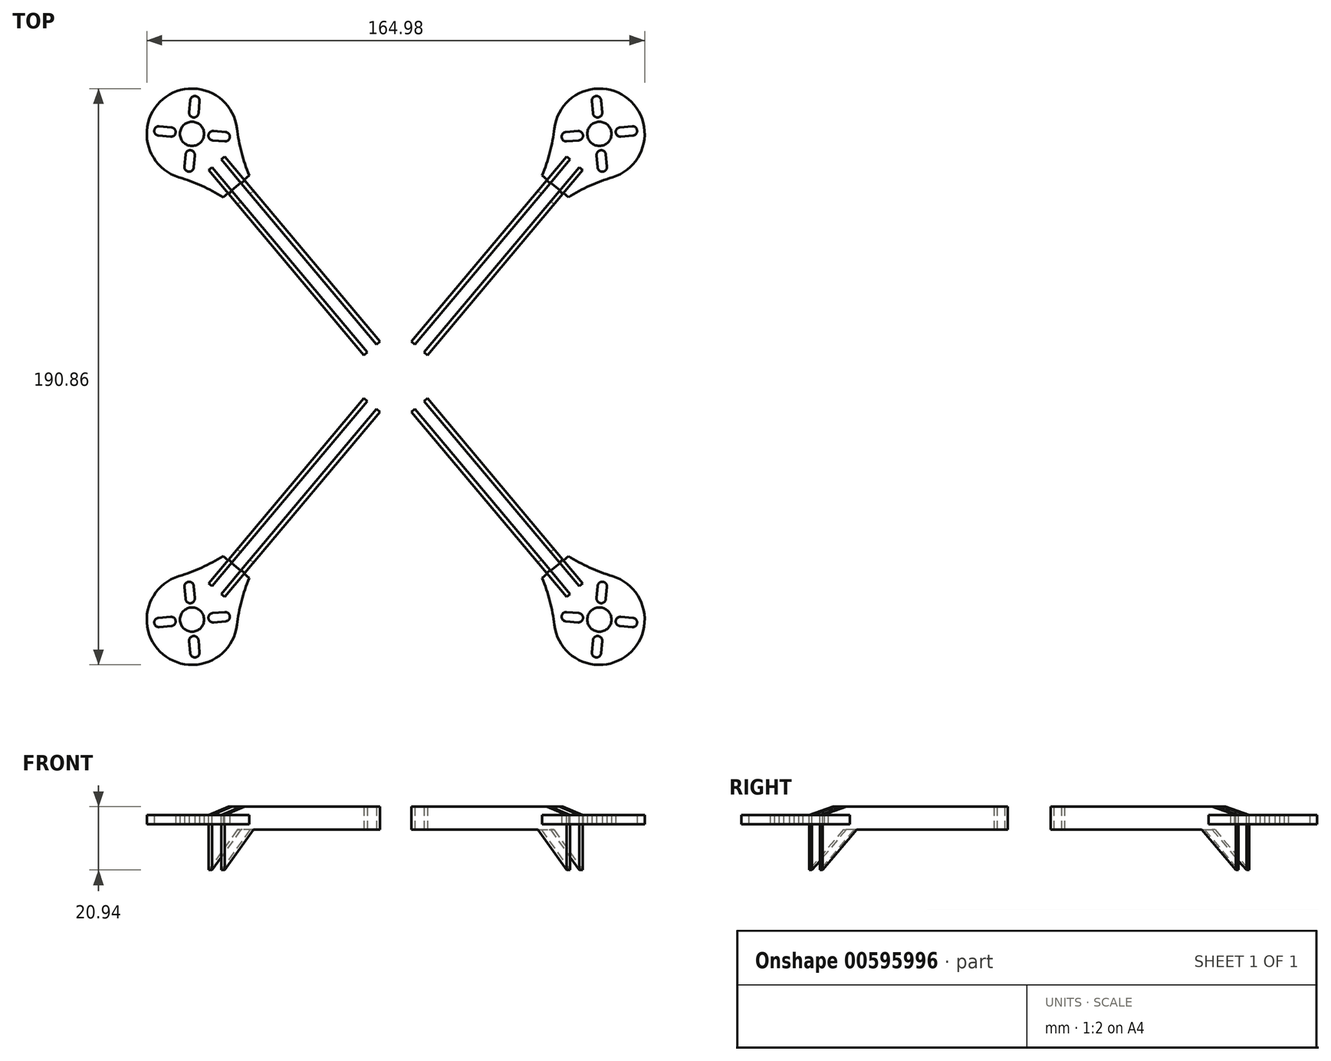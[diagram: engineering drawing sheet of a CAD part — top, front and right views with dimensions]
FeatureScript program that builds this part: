
annotation { "Feature Type Name" : "Feature", "Feature Type Description" : "" }
export const myFeature = defineFeature(function(context is Context, id is Id, definition is map)
    precondition{}
    {
        {
            var Q0;
            Q0=qCreatedBy(makeId("Top.planeOp"),FACE);
            var sketch = newSketch(context, id + "F0", { "sketchPlane" : qUnion([Q0])});
            skCircle(sketch, "E0", {"center": v(0, 0) * mm, "radius": 105 * mm, "construction": true});
            skLineSegment(sketch, "E1", {"start": v(0, 0) * mm, "end": v(0, 150) * mm, "construction": true});
            skLineSegment(sketch, "E2", {"start": v(0, 0) * mm, "end": v(160.43, 0) * mm, "construction": true});
            skLineSegment(sketch, "E3", {"start": v(0, 0) * mm, "end": v(101.52, 121) * mm, "construction": true});
            skCircle(sketch, "E4", {"center": v(67.5, 80.43) * mm, "radius": 63.5 * mm, "construction": true});
            skSolve(sketch);
        }
        {
            var Q0;
            Q0=sQuery(id+"F0.wireOp",EDGE,"E3");
            cPlane(context, id + "F1", {"entities" : qUnion([Q0]), "cplaneType" : CPlaneType.LINE_ANGLE, "offset" : 25 * mm, "angle" : 90 * degree, "width" : 150 * mm, "height" : 150 * mm});
        }
        {
            var Q0;
            Q0=qCreatedBy(id+"F1.planeOp",FACE);
            cPlane(context, id + "F2", {"entities" : qUnion([Q0]), "cplaneType" : CPlaneType.OFFSET, "offset" : 2 * mm, "width" : 150 * mm, "height" : 150 * mm});
        }
        {
            var Q0;
            Q0=qCreatedBy(id+"F2.planeOp",FACE);
            var sketch = newSketch(context, id + "F3", { "sketchPlane" : qUnion([Q0])});
            skLineSegment(sketch, "E5", {"start": v(12.3, 5.77) * mm, "end": v(12.3, -1.84) * mm});
            skLineSegment(sketch, "E6", {"start": v(12.3, -1.84) * mm, "end": v(77.46, -1.84) * mm});
            skLineSegment(sketch, "E7", {"start": v(77.46, -1.84) * mm, "end": v(92.25, -15.17) * mm});
            skLineSegment(sketch, "E8", {"start": v(92.25, -15.17) * mm, "end": v(92.25, 3) * mm});
            skLineSegment(sketch, "E9", {"start": v(81.96, 5.77) * mm, "end": v(12.3, 5.77) * mm});
            skLineSegment(sketch, "E10", {"start": v(92.25, 3) * mm, "end": v(81.96, 5.77) * mm});
            skSolve(sketch);
        }
        {
            var Q0;
            Q0=qCreatedBy(makeId("Top.planeOp"),FACE);
            var sketch = newSketch(context, id + "F4", { "sketchPlane" : qUnion([Q0])});
            skCircle(sketch, "E11", {"center": v(67.5, 80.43) * mm, "radius": 15 * mm});
            skArc(sketch, "E12", {"start": v(71.84, 66.08) * mm, "mid": v(64.3, 63.23) * mm, "end": v(57.22, 59.4) * mm});
            skLineSegment(sketch, "E13", {"start": v(57.22, 59.4) * mm, "end": v(52.89, 63.03) * mm});
            skLineSegment(sketch, "E14.0", {"start": v(52.89, 63.03) * mm, "end": v(57.85, 68.94) * mm});
            skPoint(sketch, "E15.orphan", {"position": v(0, 0) * mm});
            skArc(sketch, "E16.MirrorCS", {"start": v(52.6, 82.22) * mm, "mid": v(51.1, 74.3) * mm, "end": v(48.56, 66.66) * mm});
            skLineSegment(sketch, "E17.MirrorCS", {"start": v(48.56, 66.66) * mm, "end": v(52.89, 63.03) * mm});
            skCircle(sketch, "E18", {"center": v(67.5, 80.43) * mm, "radius": 4 * mm});
            skLineSegment(sketch, "E19", {"start": v(67.5, 80.43) * mm, "end": v(65.8, 99.72) * mm, "construction": true});
            skLineSegment(sketch, "E20", {"start": v(64.99, 91.26) * mm, "end": v(65.34, 87.27) * mm});
            skLineSegment(sketch, "E21", {"start": v(65.34, 87.27) * mm, "end": v(68.43, 87.54) * mm, "construction": true});
            skLineSegment(sketch, "E22", {"start": v(68.43, 87.54) * mm, "end": v(68.08, 91.53) * mm});
            skLineSegment(sketch, "E23", {"start": v(68.08, 91.53) * mm, "end": v(64.99, 91.26) * mm, "construction": true});
            skArc(sketch, "E24", {"start": v(68.08, 91.53) * mm, "mid": v(66.4, 92.94) * mm, "end": v(64.99, 91.26) * mm});
            skArc(sketch, "E25", {"start": v(65.34, 87.27) * mm, "mid": v(67.02, 85.86) * mm, "end": v(68.43, 87.54) * mm});
            skArc(sketch, "E26.1.0", {"start": v(60.65, 78.28) * mm, "mid": v(62.06, 79.96) * mm, "end": v(60.38, 81.37) * mm});
            skLineSegment(sketch, "E26.1.1", {"start": v(56.67, 77.93) * mm, "end": v(60.65, 78.28) * mm});
            skArc(sketch, "E26.1.2", {"start": v(56.4, 81.02) * mm, "mid": v(55, 79.34) * mm, "end": v(56.67, 77.93) * mm});
            skLineSegment(sketch, "E26.1.3", {"start": v(60.65, 78.28) * mm, "end": v(60.38, 81.37) * mm, "construction": true});
            skLineSegment(sketch, "E26.1.4", {"start": v(56.4, 81.02) * mm, "end": v(56.67, 77.93) * mm, "construction": true});
            skLineSegment(sketch, "E26.1.5", {"start": v(60.38, 81.37) * mm, "end": v(56.4, 81.02) * mm});
            skArc(sketch, "E26.2.0", {"start": v(69.65, 73.6) * mm, "mid": v(67.97, 75) * mm, "end": v(66.56, 73.33) * mm});
            skLineSegment(sketch, "E26.2.1", {"start": v(70, 69.61) * mm, "end": v(69.65, 73.6) * mm});
            skArc(sketch, "E26.2.2", {"start": v(66.9, 69.34) * mm, "mid": v(68.59, 67.93) * mm, "end": v(70, 69.61) * mm});
            skLineSegment(sketch, "E26.2.3", {"start": v(69.65, 73.6) * mm, "end": v(66.56, 73.33) * mm, "construction": true});
            skLineSegment(sketch, "E26.2.4", {"start": v(66.9, 69.34) * mm, "end": v(70, 69.61) * mm, "construction": true});
            skLineSegment(sketch, "E26.2.5", {"start": v(66.56, 73.33) * mm, "end": v(66.9, 69.34) * mm});
            skArc(sketch, "E26.3.0", {"start": v(74.33, 82.59) * mm, "mid": v(72.92, 80.9) * mm, "end": v(74.6, 79.5) * mm});
            skLineSegment(sketch, "E26.3.1", {"start": v(78.32, 82.94) * mm, "end": v(74.33, 82.59) * mm});
            skArc(sketch, "E26.3.2", {"start": v(78.59, 79.85) * mm, "mid": v(80, 81.53) * mm, "end": v(78.32, 82.94) * mm});
            skLineSegment(sketch, "E26.3.3", {"start": v(74.33, 82.59) * mm, "end": v(74.6, 79.5) * mm, "construction": true});
            skLineSegment(sketch, "E26.3.4", {"start": v(78.59, 79.85) * mm, "end": v(78.32, 82.94) * mm, "construction": true});
            skLineSegment(sketch, "E26.3.5", {"start": v(74.6, 79.5) * mm, "end": v(78.59, 79.85) * mm});
            skSolve(sketch);
        }
        {
            var Q0;
            Q0 = qSketchRegion(id + "F4", true);
            extrude(context, id + "F5", {"entities" : qUnion([Q0]), "depth" : 3 * mm, "offsetDistance" : 25 * mm});
        }
        {
            var Q0;
            Q0 = qSketchRegion(id + "F3", true);
            extrude(context, id + "F6", {"entities" : qUnion([Q0]), "depth" : 1.5 * mm, "offsetDistance" : 25 * mm});
        }
        {
            var Q0;
            Q0=makeQuery(id+"F6.opExtrude","SWEPT_BODY",BODY,{"disambiguationData":[OSD([sQuery(id+"F3.wireOp",EDGE,"E5"),sQuery(id+"F3.wireOp",EDGE,"E6"),sQuery(id+"F3.wireOp",EDGE,"E7"),sQuery(id+"F3.wireOp",EDGE,"E8"),sQuery(id+"F3.wireOp",EDGE,"E9")])]});
            var Q1;
            Q1=qCreatedBy(id+"F1.planeOp",FACE);
            mirror(context, id + "F7", {"entities" : qUnion([Q0]), "mirrorPlane" : qUnion([Q1])});
        }
        {
            var Q0;
            Q0=makeQuery(id+"F6.opExtrude","SWEPT_BODY",BODY,{"disambiguationData":[OSD([sQuery(id+"F3.wireOp",EDGE,"E5"),sQuery(id+"F3.wireOp",EDGE,"E6"),sQuery(id+"F3.wireOp",EDGE,"E7"),sQuery(id+"F3.wireOp",EDGE,"E8"),sQuery(id+"F3.wireOp",EDGE,"E9")])]});
            var Q1;
            Q1=makeQuery(id+"F7.opPattern","COPY",BODY,{"derivedFrom":makeQuery(id+"F6.opExtrude","SWEPT_BODY",BODY,{"disambiguationData":[OSD([sQuery(id+"F3.wireOp",EDGE,"E5"),sQuery(id+"F3.wireOp",EDGE,"E6"),sQuery(id+"F3.wireOp",EDGE,"E7"),sQuery(id+"F3.wireOp",EDGE,"E8"),sQuery(id+"F3.wireOp",EDGE,"E9")])]}),"instanceName":"1"});
            var Q2;
            Q2=makeQuery(id+"F5.opExtrude","SWEPT_BODY",BODY,{"disambiguationData":[OSD([sQuery(id+"F4.wireOp",EDGE,"E11")])]});
            var Q3;
            Q3=qCreatedBy(makeId("Right.planeOp"),FACE);
            mirror(context, id + "F8", {"entities" : qUnion([Q0, Q1, Q2]), "mirrorPlane" : qUnion([Q3])});
        }
        {
            var Q0;
            Q0=makeQuery(id+"F8.opPattern","COPY",BODY,{"derivedFrom":makeQuery(id+"F5.opExtrude","SWEPT_BODY",BODY,{"disambiguationData":[OSD([sQuery(id+"F4.wireOp",EDGE,"E11")])]}),"instanceName":"1"});
            var Q1;
            Q1=makeQuery(id+"F5.opExtrude","SWEPT_BODY",BODY,{"disambiguationData":[OSD([sQuery(id+"F4.wireOp",EDGE,"E11")])]});
            var Q2;
            Q2=makeQuery(id+"F8.opPattern","COPY",BODY,{"derivedFrom":makeQuery(id+"F6.opExtrude","SWEPT_BODY",BODY,{"disambiguationData":[OSD([sQuery(id+"F3.wireOp",EDGE,"E5"),sQuery(id+"F3.wireOp",EDGE,"E6"),sQuery(id+"F3.wireOp",EDGE,"E7"),sQuery(id+"F3.wireOp",EDGE,"E8"),sQuery(id+"F3.wireOp",EDGE,"E9")])]}),"instanceName":"1"});
            var Q3;
            Q3=makeQuery(id+"F8.opPattern","COPY",BODY,{"derivedFrom":makeQuery(id+"F7.opPattern","COPY",BODY,{"derivedFrom":makeQuery(id+"F6.opExtrude","SWEPT_BODY",BODY,{"disambiguationData":[OSD([sQuery(id+"F3.wireOp",EDGE,"E5"),sQuery(id+"F3.wireOp",EDGE,"E6"),sQuery(id+"F3.wireOp",EDGE,"E7"),sQuery(id+"F3.wireOp",EDGE,"E8"),sQuery(id+"F3.wireOp",EDGE,"E9")])]}),"instanceName":"1"}),"instanceName":"1"});
            var Q4;
            Q4=makeQuery(id+"F7.opPattern","COPY",BODY,{"derivedFrom":makeQuery(id+"F6.opExtrude","SWEPT_BODY",BODY,{"disambiguationData":[OSD([sQuery(id+"F3.wireOp",EDGE,"E5"),sQuery(id+"F3.wireOp",EDGE,"E6"),sQuery(id+"F3.wireOp",EDGE,"E7"),sQuery(id+"F3.wireOp",EDGE,"E8"),sQuery(id+"F3.wireOp",EDGE,"E9")])]}),"instanceName":"1"});
            var Q5;
            Q5=makeQuery(id+"F6.opExtrude","SWEPT_BODY",BODY,{"disambiguationData":[OSD([sQuery(id+"F3.wireOp",EDGE,"E5"),sQuery(id+"F3.wireOp",EDGE,"E6"),sQuery(id+"F3.wireOp",EDGE,"E7"),sQuery(id+"F3.wireOp",EDGE,"E8"),sQuery(id+"F3.wireOp",EDGE,"E9")])]});
            var Q6;
            Q6=qCreatedBy(makeId("Front.planeOp"),FACE);
            mirror(context, id + "F9", {"entities" : qUnion([Q0, Q1, Q2, Q3, Q4, Q5]), "mirrorPlane" : qUnion([Q6])});
        }
    });
